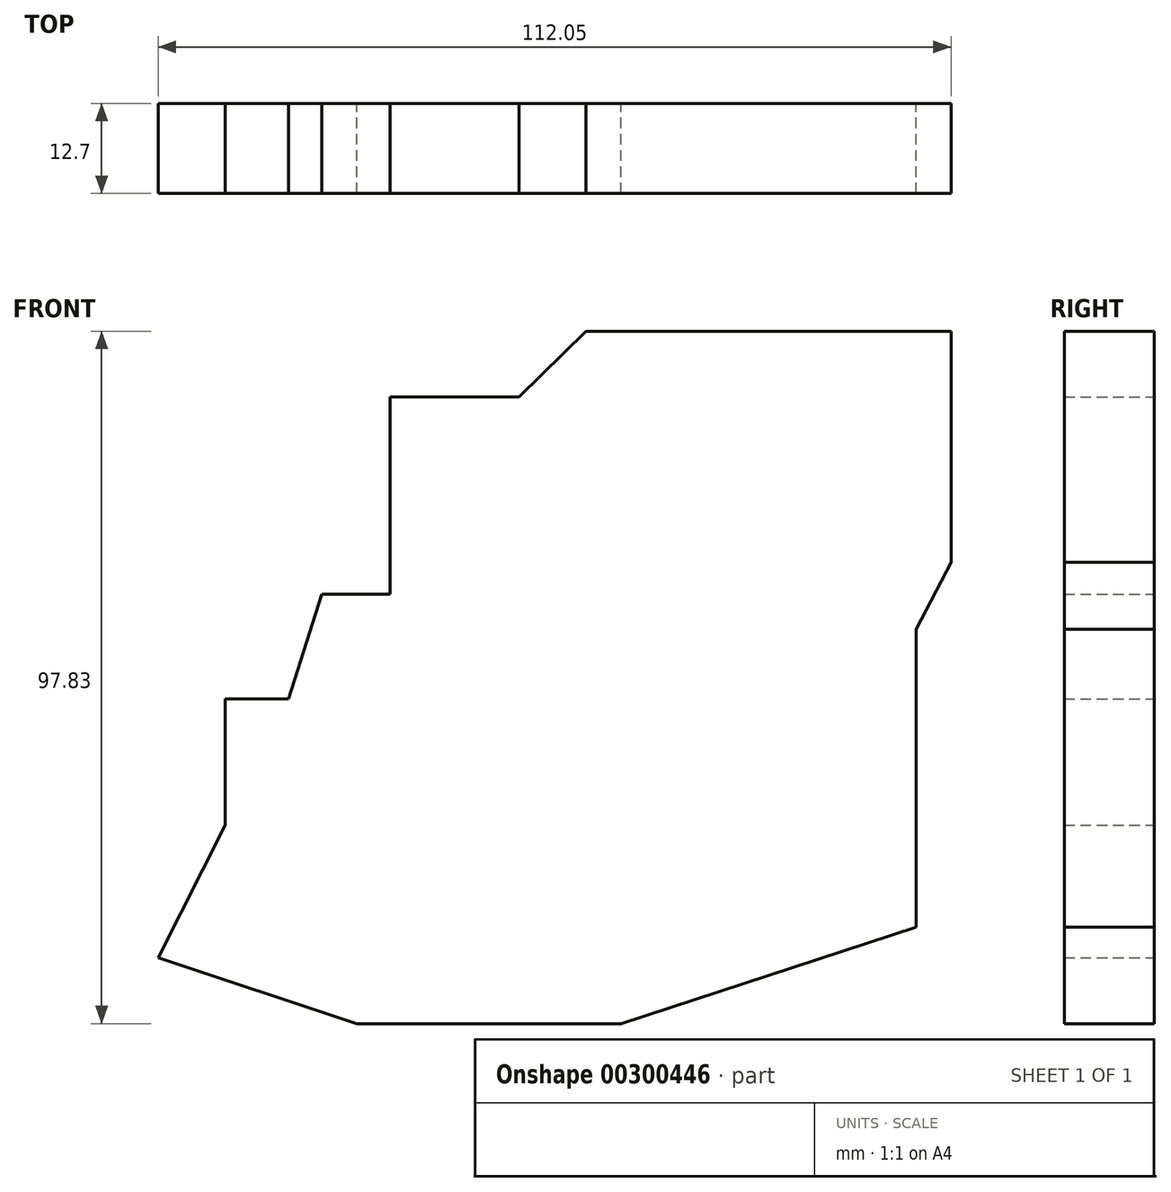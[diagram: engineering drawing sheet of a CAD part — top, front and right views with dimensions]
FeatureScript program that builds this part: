
annotation { "Feature Type Name" : "Feature", "Feature Type Description" : "" }
export const myFeature = defineFeature(function(context is Context, id is Id, definition is map)
    precondition{}
    {
        {
            var Q0;
            Q0=qCreatedBy(makeId("Front.planeOp"),FACE);
            var sketch = newSketch(context, id + "F0", { "sketchPlane" : qUnion([Q0])});
            skLineSegment(sketch, "E0", {"start": v(-54.98, -36.6) * mm, "end": v(-26.92, -45.88) * mm});
            skLineSegment(sketch, "E1", {"start": v(-26.92, -45.88) * mm, "end": v(10.43, -45.88) * mm});
            skLineSegment(sketch, "E2", {"start": v(10.43, -45.88) * mm, "end": v(52.14, -32.23) * mm});
            skLineSegment(sketch, "E3", {"start": v(52.14, -32.23) * mm, "end": v(52.14, 9.86) * mm});
            skLineSegment(sketch, "E4", {"start": v(52.14, 9.86) * mm, "end": v(57.07, 19.34) * mm});
            skLineSegment(sketch, "E5", {"start": v(57.07, 19.34) * mm, "end": v(57.07, 51.95) * mm});
            skLineSegment(sketch, "E6", {"start": v(57.07, 51.95) * mm, "end": v(5.5, 51.95) * mm});
            skLineSegment(sketch, "E7", {"start": v(5.5, 51.95) * mm, "end": v(-3.98, 42.66) * mm});
            skLineSegment(sketch, "E8", {"start": v(-3.98, 42.66) * mm, "end": v(-22.18, 42.66) * mm});
            skLineSegment(sketch, "E9", {"start": v(-22.18, 42.66) * mm, "end": v(-22.18, 14.79) * mm});
            skLineSegment(sketch, "E10", {"start": v(-22.18, 14.79) * mm, "end": v(-31.85, 14.79) * mm});
            skLineSegment(sketch, "E11", {"start": v(-31.85, 14.79) * mm, "end": v(-36.6, 0) * mm});
            skLineSegment(sketch, "E12", {"start": v(-36.6, 0) * mm, "end": v(-45.5, 0) * mm});
            skLineSegment(sketch, "E13", {"start": v(-45.5, 0) * mm, "end": v(-45.5, -17.82) * mm});
            skLineSegment(sketch, "E14", {"start": v(-45.5, -17.82) * mm, "end": v(-54.98, -36.6) * mm});
            skSolve(sketch);
        }
        {
            var Q0;
            Q0=makeQuery(id+"F0.imprint","IMPRINT",FACE,{"disambiguationData":[TD([[makeQuery(id+"F0.imprint","IMPRINT",EDGE,{"derivedFrom":sQuery(id+"F0.wireOp",EDGE,"E0")}),1.0]])]});
            extrude(context, id + "F1", {"entities" : qUnion([Q0]), "depth" : 12.7 * mm});
        }
    });
